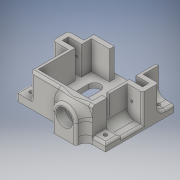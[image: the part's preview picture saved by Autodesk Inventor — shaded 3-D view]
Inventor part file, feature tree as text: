
AUTODESK INVENTOR PART (.ipt)
format: ipt  version: 2016 (Build 200138000, 138)  size: 391,680 bytes
history: native  units: in
note: dims shown in document units (in); Inventor stores cm internally (conversion verified against a paired STEP export)
features: sketch x8, other x3
ambient origin geometry x8: Origin, YZ Plane, XZ Plane, XY Plane, X Axis, Y Axis, Z Axis, Center Point
bodies: Solid1 (feature_tree)
feature tree (11):
  other  "Hip_side_part.ipt"
  other  "Solid1::Hip_side_part.ipt"
  other  "TaggingFeature1"
  sketch  "Sketch1"  dims[d0=0.3937in]
  sketch  "Sketch2"
  sketch  "Sketch3"
  sketch  "Sketch4"
  sketch  "Sketch5"
  sketch  "Sketch6"
  sketch  "Sketch7"
  sketch  "Sketch8"
